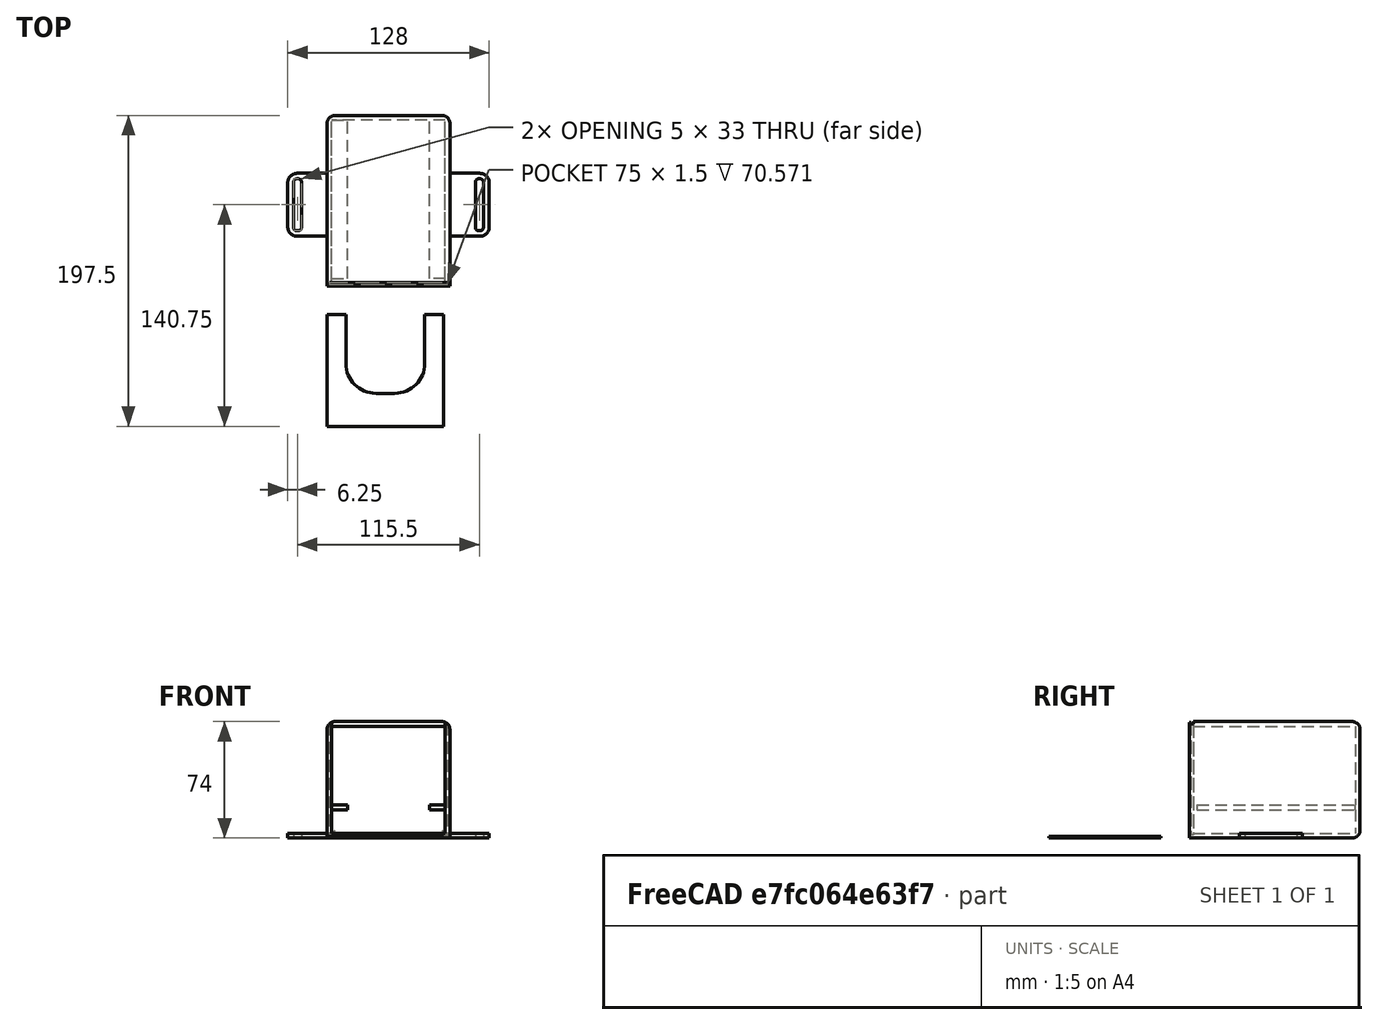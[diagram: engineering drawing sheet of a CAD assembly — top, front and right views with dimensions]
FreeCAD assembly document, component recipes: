
FREECAD ASSEMBLY — COMPONENT RECIPES ("EchoHand_circuit_case")

This assembly document has 2 components, labeled P0..P1 below (a component is one placed body or linked part). 2 of them carry a construction recipe — the FreeCAD feature program that regenerates the part from scratch, quoted from this document or its linked companion documents; the rest are supplied as boundary geometry only. No exploded tour is included for this assembly.
COMPONENT P0 — recipe-attached ("Body002", modeled in this document).
Construction recipe (the document's own serialized feature program — sketch geometry with constraints, then the solid features built on it; lengths are millimeters unless a unit is written):

FEATURE [PartDesign::FeatureBase] BaseFeature001
  BaseFeature = -> Box001
  Suppressed = false
FEATURE [Sketcher::SketchObject] Sketch014
  ArcFitTolerance = 1e-06
  AttachmentSupport = -> [BaseFeature001]
  FullyConstrained = true
  MakeInternals = false
  MapMode = 5
  Placement = pos=(0,0,1) rot=(0,0,1;0rad)
FEATURE [Sketcher::SketchObject] Sketch015
  ArcFitTolerance = 1e-06
  AttachmentSupport = -> [BaseFeature001]
  FullyConstrained = true
  MakeInternals = false
  MapMode = 5
  Placement = pos=(0,0,1) rot=(0,0,1;0rad)
FEATURE [Sketcher::SketchObject] Sketch016
  ArcFitTolerance = 1e-06
  AttachmentSupport = -> [BaseFeature001]
  ExternalGeometry = -> [BaseFeature001]
  FullyConstrained = true
  MakeInternals = false
  MapMode = 5
  Placement = pos=(0,0,1) rot=(0,0,1;0rad)
  sketch-geometry (8):
    g0: LineSegment [constr] StartX=0 StartY=71 StartZ=0 EndX=74 EndY=0 EndZ=0
    g1: LineSegment [constr] StartX=0 StartY=0 StartZ=0 EndX=74 EndY=71 EndZ=0
    g2: GeomPoint [constr] X=37 Y=35.5 Z=0
    g3: LineSegment StartX=12 StartY=21 StartZ=0 EndX=62 EndY=21 EndZ=0
    g4: LineSegment StartX=62 StartY=21 StartZ=0 EndX=62 EndY=71 EndZ=0
    g5: LineSegment StartX=62 StartY=71 StartZ=0 EndX=12 EndY=71 EndZ=0
    g6: LineSegment StartX=12 StartY=71 StartZ=0 EndX=12 EndY=21 EndZ=0
    g7: GeomPoint [constr] X=37 Y=46 Z=0
  constraints (17):
    c: Coincident(g0,g-5)
    c: Coincident(g0,g-6)
    c: Coincident(g1,g-1)
    c: Coincident(g1,g-6)
    c: Symmetric(g1,g1,g2)
    c: Coincident(g3,g4)
    c: Coincident(g4,g5)
    c: Coincident(g5,g6)
    c: Coincident(g6,g3)
    c: Horizontal(g3)
    c: Vertical(g4)
    c: Vertical(g6)
    c: Symmetric(g5,g3,g7)
    c: Distance(g4,g6) = 50
    c: Distance(g3,g5) = 50
    c: Tangent(g5,g-3)
    c: Vertical(g7,g2)
FEATURE [PartDesign::Pocket] Pocket009
  BaseFeature = -> BaseFeature001
  Direction = (0,0,-1)
  Length = 5
  Length2 = 5
  Profile = -> Sketch016
  ReferenceAxis = -> Sketch016 [N_Axis]
  Refine = true
  Suppressed = false
  Type = 1
FEATURE [PartDesign::Fillet] Fillet001
  Base = -> Pocket009 [Edge22,Edge23]
  BaseFeature = -> Pocket009
  Placement = pos=(0,5,0) rot=(0,0,1;0rad)
  Radius = 19
  Refine = true
  SupportTransform = false
  Suppressed = false
  UseAllEdges = false
FEATURE [PartDesign::Body] Body001  label="Lid"
  AllowCompound = false
  BaseFeature = -> Box001
  Group = -> [BaseFeature001,Sketch014,Sketch015,Sketch016,Pocket009,Fillet001]
  Origin = -> Origin001
  Placement = pos=(0,-89,0) rot=(0,0,1;0rad)
  Tip = -> Fillet001
COMPONENT P1 — recipe-attached ("Carapace001", modeled in this document).
Construction recipe (the document's own serialized feature program — sketch geometry with constraints, then the solid features built on it; lengths are millimeters unless a unit is written):

FEATURE [PartDesign::FeatureBase] BaseFeature
  BaseFeature = -> Box
  Suppressed = false
FEATURE [Sketcher::SketchObject] Sketch  label="Board Cutout Sketch"
  ArcFitTolerance = 1e-06
  AttachmentSupport = -> [BaseFeature]
  ExternalGeometry = -> [BaseFeature]
  FullyConstrained = true
  MakeInternals = false
  MapMode = 5
  Placement = pos=(0,0,0) rot=(1,0,0;1.5708rad)
  sketch-geometry (8):
    g0: LineSegment [constr] StartX=0 StartY=74 StartZ=0 EndX=78 EndY=0 EndZ=0
    g1: LineSegment [constr] StartX=0 StartY=0 StartZ=0 EndX=78 EndY=74 EndZ=0
    g2: GeomPoint [constr] X=39 Y=37 Z=0
    g3: LineSegment StartX=3 StartY=21 StartZ=0 EndX=75 EndY=21 EndZ=0
    g4: LineSegment StartX=75 StartY=21 StartZ=0 EndX=75 EndY=71 EndZ=0
    g5: LineSegment StartX=75 StartY=71 StartZ=0 EndX=3 EndY=71 EndZ=0
    g6: LineSegment StartX=3 StartY=71 StartZ=0 EndX=3 EndY=21 EndZ=0
    g7: GeomPoint [constr] X=39 Y=46 Z=0
  constraints (18):
    c: Coincident(g0,g-4)
    c: Coincident(g0,g-6)
    c: Coincident(g1,g-1)
    c: Coincident(g1,g-5)
    c: Symmetric(g0,g0,g2)
    c: Coincident(g3,g4)
    c: Coincident(g4,g5)
    c: Coincident(g5,g6)
    c: Coincident(g6,g3)
    c: Horizontal(g3)
    c: Horizontal(g5)
    c: Vertical(g4)
    c: Vertical(g6)
    c: Symmetric(g5,g3,g7)
    c: Distance(g3,g5) = 50
    c: Vertical(g7,g2)
    c: Distance(g5,g-4) = 3
    c: Distance(g-5,g4) = 3
FEATURE [PartDesign::Pocket] Pocket  label="Board Cutout"
  BaseFeature = -> BaseFeature
  Direction = (0,1,-2e-16)
  Length = 0
  Length2 = 5
  Offset = -3
  Profile = -> Sketch
  ReferenceAxis = -> Sketch [N_Axis]
  Refine = true
  Suppressed = false
  Type = 3
  UpToFace = -> BaseFeature [Face4]
FEATURE [Sketcher::SketchObject] Sketch001  label="Battery Cutout Sketch"
  ArcFitTolerance = 1e-06
  AttachmentSupport = -> [Pocket]
  ExternalGeometry = -> [Pocket]
  FullyConstrained = true
  MakeInternals = false
  MapMode = 5
  Placement = pos=(0,0,0) rot=(1,0,0;1.5708rad)
  sketch-geometry (8):
    g0: LineSegment [constr] StartX=0 StartY=74 StartZ=0 EndX=78 EndY=0 EndZ=0
    g1: LineSegment [constr] StartX=0 StartY=0 StartZ=0 EndX=78 EndY=74 EndZ=0
    g2: GeomPoint [constr] X=39 Y=37 Z=0
    g3: LineSegment StartX=3 StartY=3 StartZ=0 EndX=75 EndY=3 EndZ=0
    g4: LineSegment StartX=75 StartY=3 StartZ=0 EndX=75 EndY=18 EndZ=0
    g5: LineSegment StartX=75 StartY=18 StartZ=0 EndX=3 EndY=18 EndZ=0
    g6: LineSegment StartX=3 StartY=18 StartZ=0 EndX=3 EndY=3 EndZ=0
    g7: GeomPoint [constr] X=39 Y=10.5 Z=0
  constraints (18):
    c: Coincident(g0,g-4)
    c: Coincident(g0,g-6)
    c: Coincident(g1,g-1)
    c: Coincident(g1,g-5)
    c: Symmetric(g1,g1,g2)
    c: Coincident(g3,g4)
    c: Coincident(g4,g5)
    c: Coincident(g5,g6)
    c: Coincident(g6,g3)
    c: Horizontal(g3)
    c: Horizontal(g5)
    c: Vertical(g4)
    c: Vertical(g6)
    c: Symmetric(g5,g3,g7)
    c: Distance(g3,g5) = 15
    c: Vertical(g7,g2)
    c: Distance(g-6,g3) = 3
    c: Distance(g-5,g4) = 3
FEATURE [PartDesign::Pocket] Pocket001  label="Battery Cutout"
  BaseFeature = -> Pocket
  Direction = (0,1,-2e-16)
  Length = 0
  Length2 = 5
  Profile = -> Sketch001
  ReferenceAxis = -> Sketch001 [N_Axis]
  Refine = true
  Suppressed = false
  Type = 3
  UpToFace = -> Pocket [Face11]
FEATURE [Sketcher::SketchObject] Sketch002
  ArcFitTolerance = 1e-06
  AttachmentSupport = -> [Pocket001]
  ExternalGeometry = -> [Pocket001]
  FullyConstrained = true
  MakeInternals = false
  MapMode = 5
  Placement = pos=(0,0,0) rot=(1,0,0;1.5708rad)
  sketch-geometry (6):
    g0: LineSegment [constr] StartX=39 StartY=74 StartZ=0 EndX=39 EndY=0 EndZ=0
    g1: LineSegment StartX=13 StartY=18 StartZ=0 EndX=65 EndY=18 EndZ=0
    g2: LineSegment StartX=65 StartY=18 StartZ=0 EndX=65 EndY=21 EndZ=0
    g3: LineSegment StartX=65 StartY=21 StartZ=0 EndX=13 EndY=21 EndZ=0
    g4: LineSegment StartX=13 StartY=21 StartZ=0 EndX=13 EndY=18 EndZ=0
    g5: GeomPoint [constr] X=39 Y=19.5 Z=0
  constraints (14):
    c: Symmetric(g-3,g-3,g0)
    c: Symmetric(g-6,g-6,g0)
    c: Coincident(g1,g2)
    c: Coincident(g2,g3)
    c: Coincident(g3,g4)
    c: Coincident(g4,g1)
    c: Horizontal(g3)
    c: Vertical(g2)
    c: Vertical(g4)
    c: Symmetric(g3,g1,g5)
    c: PointOnObject(g5,g0)
    c: PointOnObject(g2,g-7)
    c: Tangent(g1,g-8)
    c: DistanceX(g2,g-7) = 10
FEATURE [PartDesign::Pocket] Pocket002  label="Center Cutout"
  BaseFeature = -> Pocket001
  Direction = (0,1,-2e-16)
  Length = 0
  Length2 = 5
  Profile = -> Sketch002
  ReferenceAxis = -> Sketch002 [N_Axis]
  Refine = true
  Suppressed = false
  Type = 3
  UpToFace = -> Pocket001 [Face16]
FEATURE [Sketcher::SketchObject] Sketch008
  ArcFitTolerance = 1e-06
  AttachmentSupport = -> [Pocket002]
  ExternalGeometry = -> [Pocket002]
  FullyConstrained = true
  MakeInternals = false
  MapMode = 5
  Placement = pos=(0,0,74) rot=(0,0,1;0rad)
  sketch-geometry (6):
    g0: LineSegment [constr] StartX=39 StartY=108.5 StartZ=0 EndX=39 EndY=0 EndZ=0
    g1: LineSegment StartX=1.5 StartY=1 StartZ=0 EndX=76.5 EndY=1 EndZ=0
    g2: LineSegment StartX=76.5 StartY=1 StartZ=0 EndX=76.5 EndY=2.5 EndZ=0
    g3: LineSegment StartX=76.5 StartY=2.5 StartZ=0 EndX=1.5 EndY=2.5 EndZ=0
    g4: LineSegment StartX=1.5 StartY=2.5 StartZ=0 EndX=1.5 EndY=1 EndZ=0
    g5: GeomPoint [constr] X=39 Y=1.75 Z=0
  constraints (15):
    c: Symmetric(g-4,g-4,g0)
    c: Symmetric(g-3,g-3,g0)
    c: Coincident(g1,g2)
    c: Coincident(g2,g3)
    c: Coincident(g3,g4)
    c: Coincident(g4,g1)
    c: Horizontal(g1)
    c: Horizontal(g3)
    c: Vertical(g2)
    c: Vertical(g4)
    c: Symmetric(g3,g1,g5)
    c: PointOnObject(g5,g0)
    c: Distance(g-3,g1) = 1
    c: Distance(g1,g3) = 1.5
    c: Distance(g-2,g4) = 1.5
FEATURE [PartDesign::Pocket] Pocket005
  BaseFeature = -> Pocket002
  Direction = (0,0,-1)
  Length = 0
  Length2 = 5
  Offset = 1
  Profile = -> Sketch008
  ReferenceAxis = -> Sketch008 [N_Axis]
  Refine = true
  Suppressed = false
  Type = 3
  UpToFace = -> Pocket002 [Face17]
FEATURE [Sketcher::SketchObject] Sketch009
  ArcFitTolerance = 1e-06
  AttachmentSupport = -> [Pocket005]
  ExternalGeometry = -> [Pocket005]
  FullyConstrained = true
  MakeInternals = false
  MapMode = 5
  Placement = pos=(0,0,0) rot=(1,0,0;1.5708rad)
  sketch-geometry (4):
    g0: LineSegment StartX=13 StartY=18 StartZ=0 EndX=13 EndY=21 EndZ=0
    g1: LineSegment StartX=13 StartY=21 StartZ=0 EndX=3 EndY=21 EndZ=0
    g2: LineSegment StartX=3 StartY=21 StartZ=0 EndX=3 EndY=18 EndZ=0
    g3: LineSegment StartX=3 StartY=18 StartZ=0 EndX=13 EndY=18 EndZ=0
  constraints (10):
    c: Coincident(g0,g1)
    c: Coincident(g1,g2)
    c: Coincident(g2,g3)
    c: Coincident(g3,g0)
    c: Vertical(g0)
    c: Vertical(g2)
    c: Horizontal(g1)
    c: Horizontal(g3)
    c: Coincident(g0,g-3)
    c: Coincident(g1,g-4)
FEATURE [PartDesign::Pocket] Pocket006
  BaseFeature = -> Pocket005
  Direction = (0,1,-2e-16)
  Length = 5
  Length2 = 5
  Profile = -> Sketch009
  ReferenceAxis = -> Sketch009 [N_Axis]
  Refine = true
  Suppressed = false
  Type = 0
FEATURE [Sketcher::SketchObject] Sketch010
  ArcFitTolerance = 1e-06
  AttachmentSupport = -> [Pocket006]
  ExternalGeometry = -> [Pocket006]
  FullyConstrained = true
  MakeInternals = false
  MapMode = 5
  Placement = pos=(0,0,0) rot=(1,0,0;1.5708rad)
  sketch-geometry (4):
    g0: LineSegment StartX=65 StartY=18 StartZ=0 EndX=75 EndY=18 EndZ=0
    g1: LineSegment StartX=75 StartY=18 StartZ=0 EndX=75 EndY=21 EndZ=0
    g2: LineSegment StartX=75 StartY=21 StartZ=0 EndX=65 EndY=21 EndZ=0
    g3: LineSegment StartX=65 StartY=21 StartZ=0 EndX=65 EndY=18 EndZ=0
  constraints (10):
    c: Coincident(g0,g1)
    c: Coincident(g1,g2)
    c: Coincident(g2,g3)
    c: Coincident(g3,g0)
    c: Horizontal(g0)
    c: Horizontal(g2)
    c: Vertical(g1)
    c: Vertical(g3)
    c: Coincident(g0,g-3)
    c: Coincident(g1,g-4)
FEATURE [PartDesign::Pocket] Pocket007
  BaseFeature = -> Pocket006
  Direction = (0,1,-2e-16)
  Length = 5
  Length2 = 5
  Profile = -> Sketch010
  ReferenceAxis = -> Sketch010 [N_Axis]
  Refine = true
  Suppressed = false
  Type = 0
FEATURE [Sketcher::SketchObject] Sketch011
  ArcFitTolerance = 1e-06
  AttachmentSupport = -> [Pocket007]
  ExternalGeometry = -> [Pocket007]
  FullyConstrained = true
  MakeInternals = false
  MapMode = 5
  Placement = pos=(0,0,0) rot=(1,0,0;1.5708rad)
  sketch-geometry (6):
    g0: LineSegment [constr] StartX=3 StartY=71 StartZ=0 EndX=3 EndY=74 EndZ=0
    g1: LineSegment [constr] StartX=75 StartY=71 StartZ=0 EndX=75 EndY=74 EndZ=0
    g2: LineSegment StartX=3 StartY=71 StartZ=0 EndX=75 EndY=71 EndZ=0
    g3: LineSegment StartX=75 StartY=71 StartZ=0 EndX=75 EndY=74 EndZ=0
    g4: LineSegment StartX=75 StartY=74 StartZ=0 EndX=3 EndY=74 EndZ=0
    g5: LineSegment StartX=3 StartY=74 StartZ=0 EndX=3 EndY=71 EndZ=0
  constraints (16):
    c: Coincident(g0,g-3)
    c: PointOnObject(g0,g-4)
    c: Vertical(g0)
    c: Coincident(g1,g-5)
    c: PointOnObject(g1,g-4)
    c: Vertical(g1)
    c: Coincident(g2,g3)
    c: Coincident(g3,g4)
    c: Coincident(g4,g5)
    c: Coincident(g5,g2)
    c: Horizontal(g2)
    c: Horizontal(g4)
    c: Vertical(g3)
    c: Vertical(g5)
    c: Coincident(g2,g0)
    c: Coincident(g3,g1)
FEATURE [PartDesign::Pocket] Pocket008
  BaseFeature = -> Pocket007
  Direction = (0,1,-2e-16)
  Length = 2.5
  Length2 = 5
  Profile = -> Sketch011
  ReferenceAxis = -> Sketch011 [N_Axis]
  Refine = true
  Suppressed = false
  Type = 0
FEATURE [Sketcher::SketchObject] Sketch012
  ArcFitTolerance = 1e-06
  AttachmentSupport = -> [Pocket008]
  ExternalGeometry = -> [Pocket008]
  FullyConstrained = false
  MakeInternals = false
  MapMode = 5
  Placement = pos=(0,0,74) rot=(0,0,1;0rad)
  sketch-geometry (46):
    g0: LineSegment [constr] StartX=0 StartY=108.5 StartZ=0 EndX=78 EndY=108.5 EndZ=0
    g1: LineSegment [constr] StartX=0 StartY=72.3333 StartZ=0 EndX=78 EndY=72.3333 EndZ=0
    g2: LineSegment [constr] StartX=0 StartY=36.1667 StartZ=0 EndX=64.7131 EndY=36.1667 EndZ=0
    g3: LineSegment [constr] StartX=0 StartY=36.1667 StartZ=0 EndX=0 EndY=72.3333 EndZ=0
    g4: LineSegment [constr] StartX=0 StartY=72.3333 StartZ=0 EndX=0 EndY=108.5 EndZ=0
    g5: LineSegment [constr] StartX=0 StartY=0 StartZ=0 EndX=72.7151 EndY=0 EndZ=0
    g6: LineSegment [constr] StartX=0 StartY=0 StartZ=0 EndX=0 EndY=36.1667 EndZ=0
    g7: LineSegment [constr] StartX=39 StartY=108.5 StartZ=0 EndX=39 EndY=0 EndZ=0
    g8: Circle CenterX=39 CenterY=72.3333 CenterZ=0 NormalX=0 NormalY=0 NormalZ=1 AngleXU=0 Radius=25
    g9: LineSegment StartX=36.5 StartY=47.4586 StartZ=0 EndX=41.5 EndY=47.4586 EndZ=0
    g10: LineSegment StartX=41.5 StartY=47.4586 StartZ=0 EndX=41.5 EndY=97.208 EndZ=0
    g11: LineSegment StartX=41.5 StartY=97.208 StartZ=0 EndX=36.5 EndY=97.208 EndZ=0
    g12: LineSegment StartX=36.5 StartY=97.208 StartZ=0 EndX=36.5 EndY=47.4586 EndZ=0
    g13: GeomPoint [constr] X=39 Y=72.3333 Z=0
    g14: LineSegment StartX=41.5 StartY=47.4586 StartZ=0 EndX=46.5 EndY=47.4586 EndZ=0
    g15: LineSegment StartX=46.5 StartY=47.4586 StartZ=0 EndX=46.5 EndY=96.1818 EndZ=0
    g16: LineSegment StartX=46.5 StartY=96.1818 StartZ=0 EndX=41.5 EndY=96.1818 EndZ=0
    g17: LineSegment StartX=41.5 StartY=96.1818 StartZ=0 EndX=41.5 EndY=47.4586 EndZ=0
    g18: LineSegment StartX=46.5 StartY=47.4586 StartZ=0 EndX=51.5 EndY=47.4586 EndZ=0
    g19: LineSegment StartX=51.5 StartY=47.4586 StartZ=0 EndX=51.5 EndY=93.984 EndZ=0
    g20: LineSegment StartX=51.5 StartY=93.984 StartZ=0 EndX=46.5 EndY=93.984 EndZ=0
    g21: LineSegment StartX=46.5 StartY=93.984 StartZ=0 EndX=46.5 EndY=47.4586 EndZ=0
    g22: LineSegment StartX=51.5 StartY=47.4586 StartZ=0 EndX=56.5 EndY=47.4586 EndZ=0
    g23: LineSegment StartX=56.5 StartY=47.4586 StartZ=0 EndX=56.5 EndY=90.1869 EndZ=0
    g24: LineSegment StartX=56.5 StartY=90.1869 StartZ=0 EndX=51.5 EndY=90.1869 EndZ=0
    g25: LineSegment StartX=51.5 StartY=90.1869 StartZ=0 EndX=51.5 EndY=47.4586 EndZ=0
    g26: LineSegment StartX=56.5 StartY=47.4586 StartZ=0 EndX=61.5 EndY=47.4586 EndZ=0
    g27: LineSegment StartX=61.5 StartY=47.4586 StartZ=0 EndX=61.5 EndY=83.2306 EndZ=0
    g28: LineSegment StartX=61.5 StartY=83.2306 StartZ=0 EndX=56.5 EndY=83.2306 EndZ=0
    g29: LineSegment StartX=56.5 StartY=83.2306 StartZ=0 EndX=56.5 EndY=47.4586 EndZ=0
    g30: LineSegment StartX=36.5 StartY=48.0884 StartZ=0 EndX=36.5 EndY=96.1818 EndZ=0
    g31: LineSegment StartX=36.5 StartY=96.1818 StartZ=0 EndX=31.5 EndY=96.1818 EndZ=0
    g32: LineSegment StartX=31.5 StartY=96.1818 StartZ=0 EndX=31.5 EndY=48.0884 EndZ=0
    g33: LineSegment StartX=31.5 StartY=48.0884 StartZ=0 EndX=36.5 EndY=48.0884 EndZ=0
    g34: LineSegment StartX=31.5 StartY=48.0884 StartZ=0 EndX=31.5 EndY=93.984 EndZ=0
    g35: LineSegment StartX=31.5 StartY=93.984 StartZ=0 EndX=26.5 EndY=93.984 EndZ=0
    g36: LineSegment StartX=26.5 StartY=93.984 StartZ=0 EndX=26.5 EndY=48.0884 EndZ=0
    g37: LineSegment StartX=26.5 StartY=48.0884 StartZ=0 EndX=31.5 EndY=48.0884 EndZ=0
    g38: LineSegment StartX=26.5 StartY=48.0884 StartZ=0 EndX=26.5 EndY=90.1869 EndZ=0
    g39: LineSegment StartX=26.5 StartY=90.1869 StartZ=0 EndX=21.5 EndY=90.1869 EndZ=0
    g40: LineSegment StartX=21.5 StartY=90.1869 StartZ=0 EndX=21.5 EndY=48.0884 EndZ=0
    g41: LineSegment StartX=21.5 StartY=48.0884 StartZ=0 EndX=26.5 EndY=48.0884 EndZ=0
    g42: LineSegment StartX=21.5 StartY=48.0884 StartZ=0 EndX=21.5 EndY=83.2306 EndZ=0
    g43: LineSegment StartX=21.5 StartY=83.2306 StartZ=0 EndX=16.5 EndY=83.2306 EndZ=0
    g44: LineSegment StartX=16.5 StartY=83.2306 StartZ=0 EndX=16.5 EndY=48.0884 EndZ=0
    g45: LineSegment StartX=16.5 StartY=48.0884 StartZ=0 EndX=21.5 EndY=48.0884 EndZ=0
  constraints (122):
    c: PointOnObject(g1,g-2)
    c: PointOnObject(g2,g-2)
    c: Coincident(g3,g2)
    c: Coincident(g3,g1)
    c: Coincident(g4,g1)
    c: Coincident(g4,g0)
    c: Coincident(g6,g5)
    c: Coincident(g6,g2)
    c: Coincident(g5,g-1)
    c: Equal(g4,g3)
    c: Equal(g3,g6)
    c: Parallel(g1,g5)
    c: Parallel(g2,g1)
    c: Coincident(g0,g-3)
    c: Equal(g0,g1)
    c: Coincident(g0,g-4)
    c: Horizontal(g1)
    c: Symmetric(g0,g0,g7)
    c: PointOnObject(g7,g5)
    c: Vertical(g7)
    c: Diameter(g8) = 50
    c: Symmetric(g1,g1,g8)
    c: Coincident(g9,g10)
    c: Coincident(g10,g11)
    c: Coincident(g11,g12)
    c: Coincident(g12,g9)
    c: Horizontal(g9)
    c: Horizontal(g11)
    c: Vertical(g10)
    c: Vertical(g12)
    c: Symmetric(g11,g9,g13)
    c: Coincident(g13,g8)
    c: PointOnObject(g10,g8)
    c: Coincident(g14,g15)
    c: Coincident(g15,g16)
    c: Coincident(g16,g17)
    c: Coincident(g17,g14)
    c: Horizontal(g14)
    c: Horizontal(g16)
    c: Vertical(g15)
    c: Vertical(g17)
    c: Coincident(g14,g9)
    c: PointOnObject(g15,g8)
    c: Distance(g10,g12) = 5
    c: Distance(g15,g10) = 5
    c: Coincident(g18,g19)
    c: Coincident(g19,g20)
    c: Coincident(g20,g21)
    c: Coincident(g21,g18)
    c: Horizontal(g18)
    c: Horizontal(g20)
    c: Vertical(g19)
    c: Vertical(g21)
    c: Distance(g19,g21) = 5
    c: Coincident(g18,g14)
    c: PointOnObject(g19,g8)
    c: Coincident(g22,g23)
    c: Coincident(g23,g24)
    c: Coincident(g24,g25)
    c: Coincident(g25,g22)
    c: Horizontal(g22)
    c: Horizontal(g24)
    c: Vertical(g23)
    c: Vertical(g25)
    c: Distance(g23,g25) = 5
    c: Coincident(g22,g18)
    c: PointOnObject(g23,g8)
    c: Coincident(g26,g27)
    c: Coincident(g27,g28)
    c: Coincident(g28,g29)
    c: Coincident(g29,g26)
    c: Horizontal(g26)
    c: Horizontal(g28)
    c: Vertical(g27)
    c: Vertical(g29)
    c: Distance(g27,g29) = 5
    c: Coincident(g26,g22)
    c: PointOnObject(g27,g8)
    c: Coincident(g30,g31)
    c: Coincident(g31,g32)
    c: Coincident(g32,g33)
    c: Coincident(g33,g30)
    c: Vertical(g30)
    c: Vertical(g32)
    c: Horizontal(g31)
    c: Horizontal(g33)
    c: Distance(g30,g32) = 5
    c: PointOnObject(g30,g12)
    c: PointOnObject(g31,g8)
    c: Coincident(g34,g35)
    c: Coincident(g35,g36)
    c: Coincident(g36,g37)
    c: Coincident(g37,g34)
    c: Vertical(g34)
    c: Vertical(g36)
    c: Horizontal(g35)
    c: Horizontal(g37)
    c: Distance(g34,g36) = 5
    c: Coincident(g34,g32)
    c: PointOnObject(g35,g8)
    c: Coincident(g38,g39)
    c: Coincident(g39,g40)
    c: Coincident(g40,g41)
    c: Coincident(g41,g38)
    c: Vertical(g38)
    c: Vertical(g40)
    c: Horizontal(g39)
    c: Horizontal(g41)
    c: Distance(g38,g40) = 5
    c: Coincident(g38,g36)
    c: PointOnObject(g39,g8)
    c: Coincident(g42,g43)
    c: Coincident(g43,g44)
    c: Coincident(g44,g45)
    c: Coincident(g45,g42)
    c: Vertical(g42)
    c: Vertical(g44)
    c: Horizontal(g43)
    c: Horizontal(g45)
    c: Distance(g42,g44) = 5
    c: Coincident(g42,g40)
    c: PointOnObject(g43,g8)
FEATURE [PartDesign::Fillet] Fillet
  Base = -> Pocket008 [Edge12,Edge22,Edge21,Edge3,Edge13,Edge2]
  BaseFeature = -> Pocket008
  Radius = 5
  Refine = true
  SupportTransform = false
  Suppressed = false
  UseAllEdges = false
FEATURE [Sketcher::SketchObject] Sketch013
  ArcFitTolerance = 1e-06
  AttachmentSupport = -> [Fillet]
  ExternalGeometry = -> [Fillet]
  FullyConstrained = true
  MakeInternals = false
  MapMode = 5
  Placement = pos=(0,0,74) rot=(0,0,1;0rad)
  sketch-geometry (1):
    g0: LineSegment [constr] StartX=39 StartY=108.5 StartZ=0 EndX=39 EndY=0 EndZ=0
  constraints (2):
    c: Symmetric(g-4,g-4,g0)
    c: Symmetric(g-5,g-5,g0)
FEATURE [Sketcher::SketchObject] Sketch017
  ArcFitTolerance = 1e-06
  AttachmentSupport = -> [Fillet]
  FullyConstrained = true
  MakeInternals = false
  MapMode = 5
  Placement = pos=(0,0,0) rot=(1,0,0;3.14159rad)
  sketch-geometry (8):
    g0: LineSegment StartX=73 StartY=-72 StartZ=0 EndX=98 EndY=-72 EndZ=0
    g1: LineSegment StartX=98 StartY=-72 StartZ=0 EndX=98 EndY=-32 EndZ=0
    g2: LineSegment StartX=98 StartY=-32 StartZ=0 EndX=73 EndY=-32 EndZ=0
    g3: LineSegment StartX=73 StartY=-32 StartZ=0 EndX=73 EndY=-72 EndZ=0
    g4: LineSegment [constr] StartX=73 StartY=-32 StartZ=0 EndX=98 EndY=-72 EndZ=0
    g5: LineSegment [constr] StartX=73 StartY=-72 StartZ=0 EndX=98 EndY=-32 EndZ=0
    g6: GeomPoint [constr] X=85.5 Y=-52 Z=0
    g7: LineSegment [constr] StartX=85.5 StartY=-52 StartZ=0 EndX=98 EndY=-52 EndZ=0
  constraints (18):
    c: Coincident(g0,g1)
    c: Coincident(g1,g2)
    c: Coincident(g2,g3)
    c: Coincident(g3,g0)
    c: Horizontal(g0)
    c: Horizontal(g2)
    c: Vertical(g1)
    c: Tangent(g3,g-3)
    c: Distance(g1,g3) = 25
    c: Distance(g0,g2) = 40
    c: Coincident(g4,g2)
    c: Coincident(g4,g0)
    c: Coincident(g5,g0)
    c: Coincident(g5,g1)
    c: Symmetric(g4,g4,g6)
    c: Coincident(g7,g6)
    c: Symmetric(g1,g1,g7)
    c: Distance(g-4,g7) = 51.5
FEATURE [PartDesign::Plane] DatumPlane
  Length = 154.144
  MapMode = 5
  Placement = pos=(0,0,-2e-16) rot=(1,0,0;3.14159rad)
  ResizeMode = 0
  Width = 159.644
FEATURE [Sketcher::SketchObject] Sketch018
  ArcFitTolerance = 1e-06
  AttachmentSupport = -> [Fillet]
  ExternalGeometry = -> [Fillet,DatumPlane]
  FullyConstrained = false
  MakeInternals = false
  MapMode = 5
  Placement = pos=(78,0,0) rot=(0.57735,0.57735,0.57735;2.0944rad)
  sketch-geometry (13):
    g0: LineSegment StartX=31.75 StartY=3 StartZ=0 EndX=31.75 EndY=0 EndZ=0
    g1: LineSegment StartX=31.75 StartY=-2e-16 StartZ=0 EndX=71.75 EndY=-2e-16 EndZ=0
    g2: LineSegment StartX=71.75 StartY=-2e-16 StartZ=0 EndX=71.75 EndY=3 EndZ=0
    g3: LineSegment StartX=71.75 StartY=3 StartZ=0 EndX=31.75 EndY=3 EndZ=0
    g4: LineSegment [constr] StartX=31.75 StartY=3 StartZ=0 EndX=71.75 EndY=0 EndZ=0
    g5: LineSegment [constr] StartX=31.75 StartY=-2e-16 StartZ=0 EndX=71.75 EndY=3 EndZ=0
    g6: GeomPoint [constr] X=51.75 Y=1.5 Z=0
    g7: LineSegment [constr] StartX=108.5 StartY=5 StartZ=0 EndX=108.5 EndY=-5.12074 EndZ=0
    g8: LineSegment [constr] StartX=103.5 StartY=0 StartZ=0 EndX=123.61 EndY=0 EndZ=0
    g9: GeomPoint [constr] X=108.5 Y=-0.060368 Z=0
    g10: LineSegment [constr] StartX=0 StartY=69 StartZ=0 EndX=103.5 EndY=0 EndZ=0
    g11: LineSegment [constr] StartX=0 StartY=0 StartZ=0 EndX=103.5 EndY=69 EndZ=0
    g12: GeomPoint [constr] X=51.75 Y=34.5 Z=0
  constraints (26):
    c: Coincident(g0,g1)
    c: Coincident(g1,g2)
    c: Coincident(g2,g3)
    c: Coincident(g3,g0)
    c: Vertical(g0)
    c: Vertical(g2)
    c: Horizontal(g3)
    c: Distance(g0,g2) = 40
    c: Distance(g1,g3) = 3
    c: Coincident(g4,g0)
    c: Coincident(g4,g1)
    c: Coincident(g5,g0)
    c: Coincident(g5,g2)
    c: Symmetric(g4,g4,g6)
    c: Coincident(g7,g-3)
    c: Vertical(g7)
    c: Coincident(g8,g-9)
    c: Horizontal(g8)
    c: Symmetric(g7,g7,g9)
    c: Coincident(g10,g-4)
    c: Coincident(g10,g8)
    c: Coincident(g11,g-1)
    c: Coincident(g11,g-9)
    c: Symmetric(g11,g11,g12)
    c: Vertical(g6,g12)
    c: Tangent(g1,g-6)
FEATURE [PartDesign::Pad] Pad
  BaseFeature = -> Fillet
  Direction = (1,0,0)
  Length = 25
  Length2 = 10
  Profile = -> Sketch018
  ReferenceAxis = -> Sketch018 [N_Axis]
  Refine = true
  Suppressed = false
  Type = 0
FEATURE [Sketcher::SketchObject] Sketch019
  ArcFitTolerance = 1e-06
  AttachmentSupport = -> [Pad]
  ExternalGeometry = -> [Pad,DatumPlane]
  FullyConstrained = true
  MakeInternals = false
  MapMode = 5
  Placement = pos=(0,0,0) rot=(0.57735,-0.57735,-0.57735;2.0944rad)
  sketch-geometry (8):
    g0: LineSegment [constr] StartX=-103.5 StartY=69 StartZ=0 EndX=0 EndY=0 EndZ=0
    g1: LineSegment [constr] StartX=-103.5 StartY=0 StartZ=0 EndX=0 EndY=69 EndZ=0
    g2: GeomPoint [constr] X=-51.75 Y=34.5 Z=0
    g3: LineSegment StartX=-71.75 StartY=-2e-16 StartZ=0 EndX=-31.75 EndY=-2e-16 EndZ=0
    g4: LineSegment StartX=-31.75 StartY=-2e-16 StartZ=0 EndX=-31.75 EndY=3 EndZ=0
    g5: LineSegment StartX=-31.75 StartY=3 StartZ=0 EndX=-71.75 EndY=3 EndZ=0
    g6: LineSegment StartX=-71.75 StartY=3 StartZ=0 EndX=-71.75 EndY=0 EndZ=0
    g7: GeomPoint [constr] X=-51.75 Y=1.5 Z=0
  constraints (17):
    c: Coincident(g0,g-5)
    c: Coincident(g0,g-1)
    c: Coincident(g1,g-3)
    c: Coincident(g1,g-5)
    c: Symmetric(g0,g0,g2)
    c: Coincident(g3,g4)
    c: Coincident(g4,g5)
    c: Coincident(g5,g6)
    c: Coincident(g6,g3)
    c: Horizontal(g5)
    c: Vertical(g4)
    c: Vertical(g6)
    c: Symmetric(g5,g3,g7)
    c: Distance(g4,g6) = 40
    c: Distance(g3,g5) = 3
    c: Vertical(g7,g2)
    c: Tangent(g3,g-4)
FEATURE [PartDesign::Pad] Pad001
  BaseFeature = -> Pad
  Direction = (-1,0,0)
  Length = 25
  Length2 = 10
  Profile = -> Sketch019
  ReferenceAxis = -> Sketch019 [N_Axis]
  Refine = true
  Suppressed = false
  Type = 0
FEATURE [Sketcher::SketchObject] Sketch020
  ArcFitTolerance = 1e-06
  AttachmentSupport = -> [Pad001]
  ExternalGeometry = -> [Pad001]
  FullyConstrained = true
  MakeInternals = false
  MapMode = 5
  Placement = pos=(0,0,3) rot=(0,0,1;0rad)
  sketch-geometry (9):
    g0: LineSegment [constr] StartX=78 StartY=71.75 StartZ=0 EndX=103 EndY=31.75 EndZ=0
    g1: LineSegment [constr] StartX=78 StartY=31.75 StartZ=0 EndX=103 EndY=71.75 EndZ=0
    g2: GeomPoint [constr] X=90.5 Y=51.75 Z=0
    g3: LineSegment StartX=94.25 StartY=35.25 StartZ=0 EndX=99.25 EndY=35.25 EndZ=0
    g4: LineSegment StartX=99.25 StartY=35.25 StartZ=0 EndX=99.25 EndY=68.25 EndZ=0
    g5: LineSegment StartX=99.25 StartY=68.25 StartZ=0 EndX=94.25 EndY=68.25 EndZ=0
    g6: LineSegment StartX=94.25 StartY=68.25 StartZ=0 EndX=94.25 EndY=35.25 EndZ=0
    g7: GeomPoint [constr] X=96.75 Y=51.75 Z=0
    g8: GeomPoint X=103 Y=51.75 Z=0
  constraints (18):
    c: Coincident(g0,g-3)
    c: Coincident(g0,g-6)
    c: Coincident(g1,g-6)
    c: Coincident(g1,g-5)
    c: Symmetric(g1,g1,g2)
    c: Coincident(g3,g4)
    c: Coincident(g4,g5)
    c: Coincident(g5,g6)
    c: Coincident(g6,g3)
    c: Horizontal(g3)
    c: Horizontal(g5)
    c: Vertical(g4)
    c: Vertical(g6)
    c: Symmetric(g5,g3,g7)
    c: Distance(g4,g6) = 5
    c: Distance(g3,g5) = 33
    c: Symmetric(g-5,g-5,g8)
    c: Symmetric(g2,g8,g7)
FEATURE [PartDesign::Pocket] Pocket010
  BaseFeature = -> Pad001
  Direction = (0,0,-1)
  Length = 5
  Length2 = 5
  Profile = -> Sketch020
  ReferenceAxis = -> Sketch020 [N_Axis]
  Refine = true
  Suppressed = false
  Type = 1
FEATURE [Sketcher::SketchObject] Sketch021
  ArcFitTolerance = 1e-06
  AttachmentSupport = -> [Pocket010]
  ExternalGeometry = -> [Pocket010]
  FullyConstrained = true
  MakeInternals = false
  MapMode = 5
  Placement = pos=(0,0,3) rot=(0,0,1;0rad)
  sketch-geometry (9):
    g0: LineSegment [constr] StartX=-25 StartY=71.75 StartZ=0 EndX=0 EndY=31.75 EndZ=0
    g1: LineSegment [constr] StartX=-25 StartY=31.75 StartZ=0 EndX=0 EndY=71.75 EndZ=0
    g2: GeomPoint [constr] X=-12.5 Y=51.75 Z=0
    g3: LineSegment StartX=-21.25 StartY=35.25 StartZ=0 EndX=-16.25 EndY=35.25 EndZ=0
    g4: LineSegment StartX=-16.25 StartY=35.25 StartZ=0 EndX=-16.25 EndY=68.25 EndZ=0
    g5: LineSegment StartX=-16.25 StartY=68.25 StartZ=0 EndX=-21.25 EndY=68.25 EndZ=0
    g6: LineSegment StartX=-21.25 StartY=68.25 StartZ=0 EndX=-21.25 EndY=35.25 EndZ=0
    g7: GeomPoint [constr] X=-18.75 Y=51.75 Z=0
    g8: GeomPoint [constr] X=-25 Y=51.75 Z=0
  constraints (18):
    c: Coincident(g0,g-4)
    c: Coincident(g0,g-6)
    c: Coincident(g1,g-6)
    c: Coincident(g1,g-4)
    c: Symmetric(g1,g1,g2)
    c: Coincident(g3,g4)
    c: Coincident(g4,g5)
    c: Coincident(g5,g6)
    c: Coincident(g6,g3)
    c: Horizontal(g3)
    c: Horizontal(g5)
    c: Vertical(g4)
    c: Vertical(g6)
    c: Symmetric(g5,g3,g7)
    c: Distance(g4,g6) = 5
    c: Distance(g3,g5) = 33
    c: Symmetric(g-3,g-3,g8)
    c: Symmetric(g8,g2,g7)
FEATURE [PartDesign::Pocket] Pocket011
  BaseFeature = -> Pocket010
  Direction = (0,0,-1)
  Length = 5
  Length2 = 5
  Profile = -> Sketch021
  ReferenceAxis = -> Sketch021 [N_Axis]
  Refine = true
  Suppressed = false
  Type = 1
FEATURE [PartDesign::Fillet] Fillet002
  Base = -> Pocket011 [Edge95,Edge92,Edge93,Edge97,Edge89,Edge90,Edge87,Edge88]
  BaseFeature = -> Pocket011
  Radius = 2
  Refine = true
  SupportTransform = false
  Suppressed = false
  UseAllEdges = false
FEATURE [PartDesign::Fillet] Fillet003
  Base = -> Fillet002 [Edge69,Edge67,Edge65,Edge58]
  BaseFeature = -> Fillet002
  Radius = 6
  Refine = true
  SupportTransform = false
  Suppressed = false
  UseAllEdges = false
FEATURE [PartDesign::Body] Body  label="Case"
  AllowCompound = false
  BaseFeature = -> Box
  Group = -> [BaseFeature,Sketch,Pocket,Sketch001,Pocket001,Sketch002,Pocket002,Sketch008,Pocket005,Sketch009,Pocket006,Sketch010,Pocket007,Sketch011,Pocket008,Sketch012,Fillet,Sketch013,Sketch017,DatumPlane,Sketch018,Pad,Sketch019,Pad001,Sketch020,Pocket010,Sketch021,Pocket011,Fillet002,Fillet003]
  Origin = -> Origin
  Tip = -> Fillet003
PROVENANCE & LICENSES
A FreeCAD (.FCStd) document from a public repository crawl; recipes are the document's own serialized feature recipes (and, for linked parts, companion documents' recipes).
License: as declared in the source repository (recorded in the dataset sidecar).
